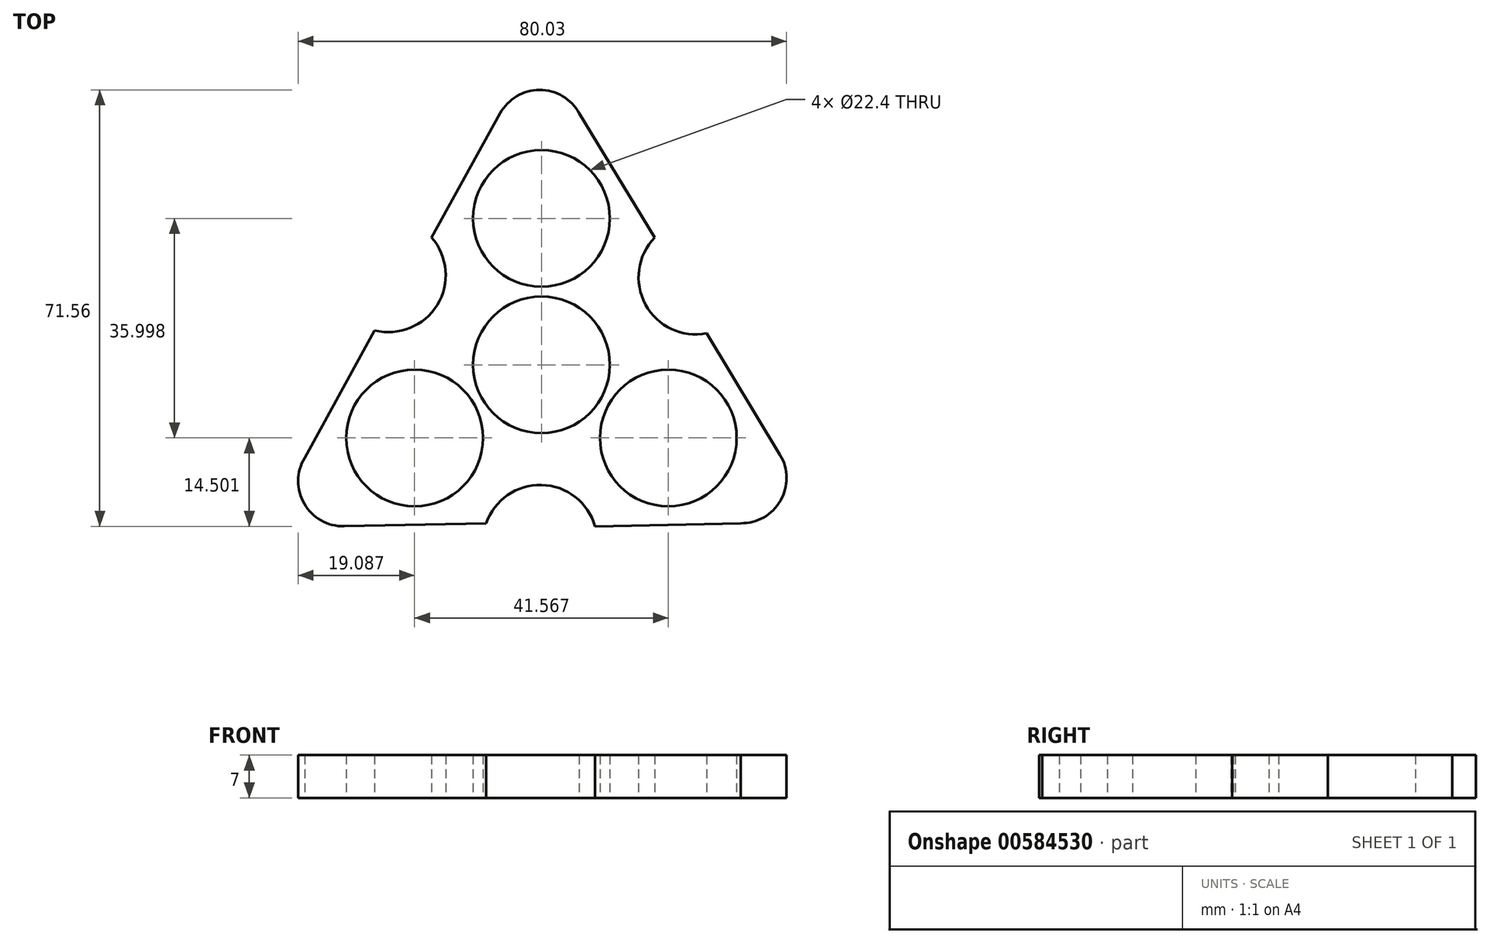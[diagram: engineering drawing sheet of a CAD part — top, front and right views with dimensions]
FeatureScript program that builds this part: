
annotation { "Feature Type Name" : "Feature", "Feature Type Description" : "" }
export const myFeature = defineFeature(function(context is Context, id is Id, definition is map)
    precondition{}
    {
        {
            var Q0;
            Q0=qCreatedBy(makeId("Top.planeOp"),FACE);
            var sketch = newSketch(context, id + "F0", { "sketchPlane" : qUnion([Q0])});
            skCircle(sketch, "E0", {"center": v(0, 0) * mm, "radius": 11.2 * mm});
            skCircle(sketch, "E1", {"center": v(0, 24) * mm, "radius": 11.2 * mm});
            skPoint(sketch, "E2.center", {"position": v(0.06, -0.2) * mm});
            skPoint(sketch, "E3.end.orphan", {"position": v(-5.32, 48.5) * mm});
            skPoint(sketch, "E4.end.orphan", {"position": v(21.3, 21) * mm});
            skPoint(sketch, "E4.start.orphan", {"position": v(4.44, 48.5) * mm});
            skCircle(sketch, "E5.1.0", {"center": v(-20.78, -12) * mm, "radius": 11.2 * mm});
            skCircle(sketch, "E5.2.0", {"center": v(20.78, -12) * mm, "radius": 11.2 * mm});
            skPoint(sketch, "E6.start.orphan", {"position": v(-21, 21) * mm});
            skArc(sketch, "E7", {"start": v(8.78, -26.5) * mm, "mid": v(0.04, -19.7) * mm, "end": v(-9.06, -26) * mm});
            skArc(sketch, "E8.1.0", {"start": v(18.56, 20.85) * mm, "mid": v(17.04, 9.88) * mm, "end": v(27.06, 5.16) * mm});
            skArc(sketch, "E8.2.0", {"start": v(-27.34, 5.65) * mm, "mid": v(-17.08, 9.82) * mm, "end": v(-18, 20.85) * mm});
            skLineSegment(sketch, "E9", {"start": v(-18, 20.85) * mm, "end": v(-6.75, 41.24) * mm});
            skLineSegment(sketch, "E10", {"start": v(18.56, 20.85) * mm, "end": v(6.18, 41.24) * mm});
            skArc(sketch, "E11", {"start": v(6.18, 41.24) * mm, "mid": v(-0.29, 45.06) * mm, "end": v(-6.75, 41.24) * mm});
            skArc(sketch, "E12.1.0", {"start": v(-38.8, -15.27) * mm, "mid": v(-38.88, -22.78) * mm, "end": v(-32.34, -26.47) * mm});
            skLineSegment(sketch, "E12.1.1", {"start": v(-9.06, -26) * mm, "end": v(-32.34, -26.47) * mm});
            skLineSegment(sketch, "E12.1.2", {"start": v(-27.34, 5.65) * mm, "end": v(-38.8, -15.27) * mm});
            skArc(sketch, "E12.2.0", {"start": v(32.63, -25.97) * mm, "mid": v(39.17, -22.28) * mm, "end": v(39.1, -14.77) * mm});
            skLineSegment(sketch, "E12.2.1", {"start": v(27.06, 5.16) * mm, "end": v(39.1, -14.77) * mm});
            skLineSegment(sketch, "E12.2.2", {"start": v(8.78, -26.5) * mm, "end": v(32.63, -25.97) * mm});
            skSolve(sketch);
        }
        {
            var Q0;
            Q0 = qSketchRegion(id + "F0", true);
            extrude(context, id + "F1", {"entities" : qUnion([Q0]), "depth" : 7 * mm, "offsetDistance" : 25 * mm});
        }
    });
